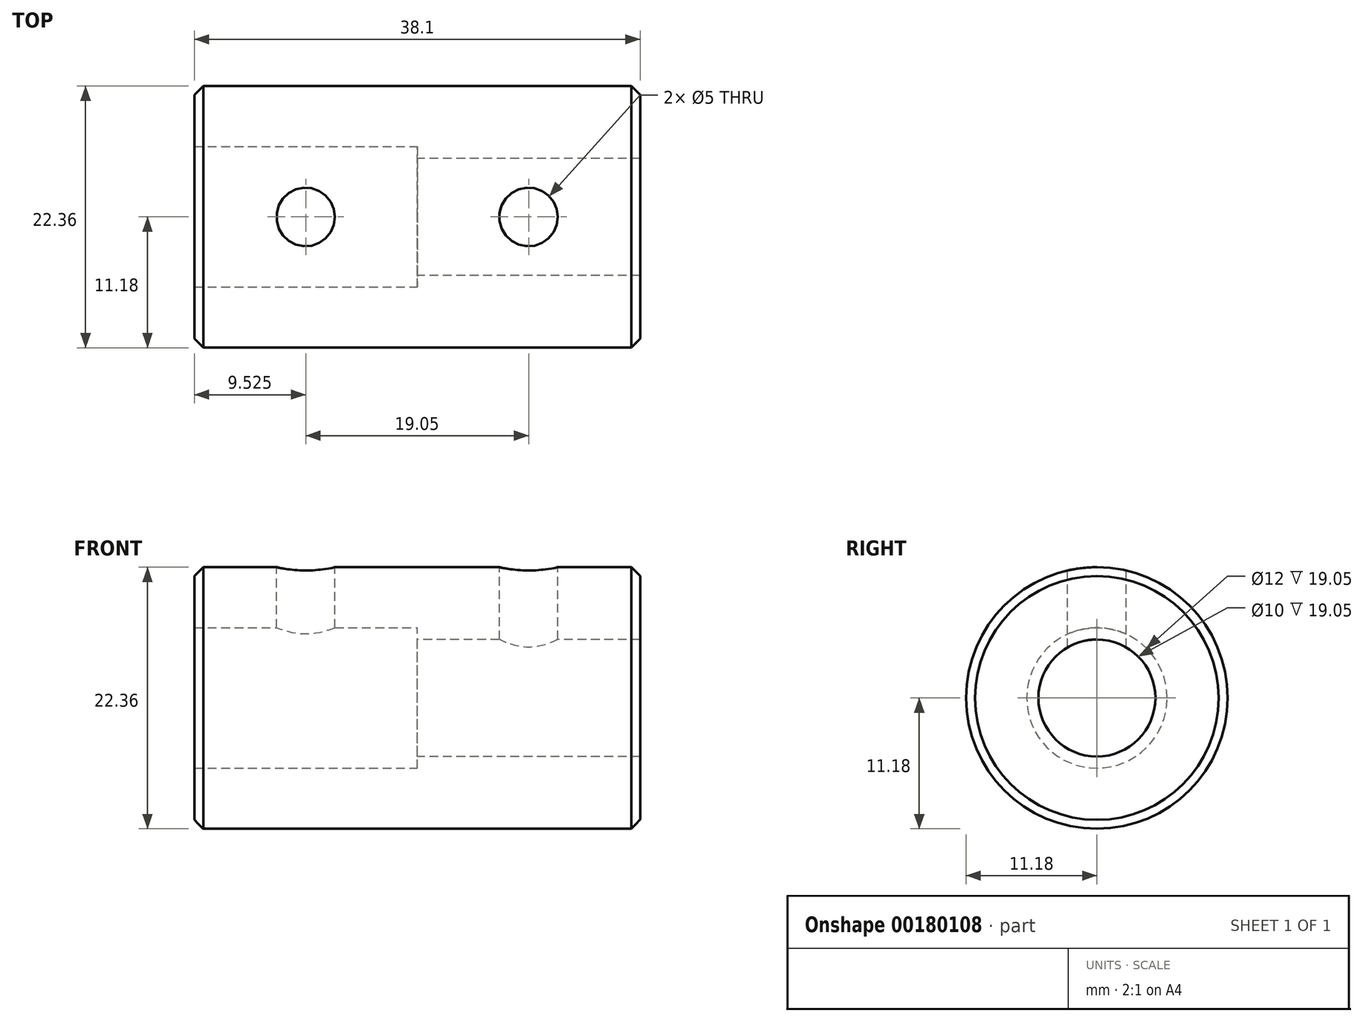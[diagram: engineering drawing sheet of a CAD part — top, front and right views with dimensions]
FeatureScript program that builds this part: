
annotation { "Feature Type Name" : "Feature", "Feature Type Description" : "" }
export const myFeature = defineFeature(function(context is Context, id is Id, definition is map)
    precondition{}
    {
        {
            var Q0;
            Q0=qCreatedBy(makeId("Right.planeOp"),FACE);
            var sketch = newSketch(context, id + "F0", { "sketchPlane" : qUnion([Q0])});
            skCircle(sketch, "E0", {"center": v(0, 0) * mm, "radius": 6 * mm});
            skCircle(sketch, "E1", {"center": v(0, 0) * mm, "radius": 11.18 * mm});
            skSolve(sketch);
        }
        {
            var Q0;
            Q0=qSketchRegion(id+"F0",true);
            extrude(context, id + "F1", {"entities" : qUnion([Q0]), "oppositeDirection" : true, "depth" : 19.05 * mm});
        }
        {
            var Q0;
            Q0=qCreatedBy(makeId("Right.planeOp"),FACE);
            var sketch = newSketch(context, id + "F2", { "sketchPlane" : qUnion([Q0])});
            skCircle(sketch, "E2.0", {"center": v(0, 0) * mm, "radius": 11.18 * mm});
            skCircle(sketch, "E3", {"center": v(0, 0) * mm, "radius": 5 * mm});
            skSolve(sketch);
        }
        {
            var Q0;
            Q0=qSketchRegion(id+"F2",true);
            extrude(context, id + "F3", {"entities" : qUnion([Q0]), "operationType" : NewBodyOperationType.ADD, "depth" : 19.05 * mm});
        }
        {
            var Q0;
            Q0=makeQuery(id+"F1.opExtrude","CAP_EDGE",EDGE,{"disambiguationData":[OSD([sQuery(id+"F0.wireOp",EDGE,"E1")])],"isStart":false});
            var Q1;
            Q1=makeQuery(id+"F3.opExtrude","CAP_EDGE",EDGE,{"disambiguationData":[OSD([sQuery(id+"F2.wireOp",EDGE,"E2.0")])],"isStart":false});
            chamfer(context, id + "F4", {"entities" : qUnion([Q0, Q1]), "width" : 0.76 * mm, "tangentPropagation" : true});
        }
        {
            var Q0;
            Q0=qCreatedBy(makeId("Top.planeOp"),FACE);
            cPlane(context, id + "F5", {"entities" : qUnion([Q0]), "cplaneType" : CPlaneType.OFFSET, "offset" : 11.18 * mm, "width" : 152.4 * mm, "height" : 152.4 * mm});
        }
        {
            var Q0;
            Q0=qCreatedBy(id+"F5.planeOp",FACE);
            var sketch = newSketch(context, id + "F6", { "sketchPlane" : qUnion([Q0])});
            skLineSegment(sketch, "E4", {"start": v(-18.29, 11.18) * mm, "end": v(18.29, 11.18) * mm, "construction": true});
            skLineSegment(sketch, "E5", {"start": v(18.29, -11.18) * mm, "end": v(-18.29, -11.18) * mm, "construction": true});
            skLineSegment(sketch, "E6.0", {"start": v(-19.05, -10.41) * mm, "end": v(-19.05, 10.41) * mm, "construction": true});
            skLineSegment(sketch, "E7.0", {"start": v(19.05, 10.41) * mm, "end": v(19.05, -10.41) * mm, "construction": true});
            skLineSegment(sketch, "E8.0", {"start": v(0, 6) * mm, "end": v(0, -6) * mm, "construction": true});
            skLineSegment(sketch, "E9", {"start": v(-46.96, 0) * mm, "end": v(42.12, 0) * mm, "construction": true});
            skLineSegment(sketch, "E10.0", {"start": v(-9.53, 6) * mm, "end": v(-9.53, -6) * mm, "construction": true});
            skLineSegment(sketch, "E11.0", {"start": v(9.53, 6) * mm, "end": v(9.53, -6) * mm, "construction": true});
            skPoint(sketch, "E12", {"position": v(-9.53, 0) * mm});
            skPoint(sketch, "E13", {"position": v(9.53, 0) * mm});
            skSolve(sketch);
        }
        {
            var Q0;
            Q0=sQuery(id+"F6.wireOp",VERTEX,"E12");
            var Q1;
            Q1=sQuery(id+"F6.wireOp",VERTEX,"E13");
            var Q2;
            Q2=makeQuery(id+"F1.opExtrude","SWEPT_BODY",BODY,{"disambiguationData":[OSD([sQuery(id+"F0.wireOp",EDGE,"E0"),sQuery(id+"F0.wireOp",EDGE,"E1")])]});
            hole(context, id + "F7", {"style" : HoleStyle.SIMPLE, "endStyle" : HoleEndStyle.BLIND, "standardTappedOrClearance" : lookupTablePath({ "standard" : "ISO", "engagement" : "75%", "pitch" : "1 mm", "size" : "M6", "type" : "Tapped" }), "standardBlindInLast" : lookupTablePath({ "standard" : "ISO", "engagement" : "75%", "pitch" : "1 mm", "size" : "M6", "type" : "Tapped" }), "holeDiameter" : 5 * mm, "holeDepth" : 12.7 * mm, "locations" : qUnion([Q0, Q1]), "scope" : qUnion([Q2]), "majorDiameter" : 6 * mm});
        }
    });
